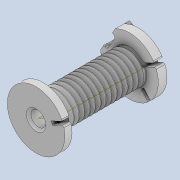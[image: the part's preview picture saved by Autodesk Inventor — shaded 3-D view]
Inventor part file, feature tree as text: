
AUTODESK INVENTOR PART (.ipt)
format: ipt  version: 2020 (Build 240168000, 168)  size: 1,136,128 bytes
history: native  units: mm
features: sketch x14, fillet x13, extrude x12, projected_geometry x12, other x4, thicken_offset x3, chamfer x2, plane x1, sweep x1, reference x1
ambient origin geometry x8: Origin, YZ Plane, XZ Plane, XY Plane, X Axis, Y Axis, Z Axis, Center Point
bodies: Solid1 (feature_tree)
feature tree (63):
  extrude  "Extrusion1"  Depth=12.0mm
  extrude  "Extrusion2"  Depth=3.0mm
  extrude  "Extrusion3"  Depth=18.0mm TaperAngle=0.0deg
  sketch  "3D Sketch1"
  plane  "Work Plane1"
  sweep  "Sweep1"
  extrude  "Extrusion4"  Depth=0.7mm
  extrude  "Extrusion5"  TaperAngle=0.0deg  [1 undecoded]
  fillet  "Fillet1"  Radius=5.0mm
  fillet  "Fillet2"  Radius=0.7mm
  fillet  "Fillet3"  Radius=1.0mm
  fillet  "Fillet4"  Radius=5.0mm
  fillet  "Fillet5"  Radius=0.7mm
  fillet  "Fillet6"  Radius=1.0mm
  extrude  "Extrusion6"  Depth=0.1mm
  thicken_offset  "Thicken1"
  thicken_offset  "Thicken2"
  extrude  "Extrusion7"  Depth=0.1mm
  extrude  "Extrusion8"  Depth=0.1mm
  extrude  "Extrusion9"  Depth=8.0mm
  chamfer  "Chamfer1"  Distance=2.0mm
  fillet  "Fillet7"  Radius=0.8mm
  fillet  "Fillet8"  Radius=0.8mm
  extrude  "Extrusion10"  Depth=0.5mm
  extrude  "Extrusion11"  Depth=0.4mm
  extrude  "Extrusion13"  Depth=0.4mm TaperAngle=0.0deg
  fillet  "Fillet10"  Radius=4.0mm
  fillet  "Fillet11"  Radius=0.8mm
  fillet  "Fillet12"  Radius=0.5mm
  fillet  "Fillet13"  Radius=0.5mm
  fillet  "Fillet14"  Radius=0.5mm
  thicken_offset  "Thicken3"
  chamfer  "Chamfer2"  Distance=3.490659mm
  sketch  "Sketch1"  dims[d0=3.0mm d1=12.0mm]
  reference  "Reference1"
  sketch  "Sketch2"  dims[d2=1.0mm d3=0.0mm d4=3.0mm]
  sketch  "Sketch3"  dims[d5=7.0mm d6=18.0mm d7=0.0mm]
  projected_geometry  "Projected Loop1"
  other  "Helical Curve2"
  sketch  "Sketch4"  dims[d8=1.0mm d9=0.0mm d14=18.0mm d15=160.0mm d16=7.0mm d17=0.0mm]
  projected_geometry  "Projected Loop2"
  projected_geometry  "Projected Loop3"
  sketch  "Sketch5"  dims[d18=0.5mm d19=0.7mm]
  projected_geometry  "Projected Loop4"
  sketch  "Sketch6"  dims[d20=0.5mm d21=0.0mm d22=0.0mm d23=5.0mm d24=0.7mm d25=1.0mm d26=0.0mm d27=5.0mm d28=0.7mm d29=1.0mm d30=0.0mm]
  projected_geometry  "Projected Loop5"
  sketch  "Sketch7"  dims[d31=1.0mm d32=0.1mm]
  projected_geometry  "Projected Loop6"
  sketch  "Sketch8"  dims[d33=0.1mm d34=0.1mm]
  projected_geometry  "Projected Loop7"
  sketch  "Sketch9"  dims[d35=1.0mm d36=0.1mm]
  projected_geometry  "Projected Loop8"
  sketch  "Sketch10"  dims[d37=30.0deg d38=8.0mm]
  projected_geometry  "Projected Loop9"
  sketch  "Sketch11"  dims[d39=6.0mm d40=2.0mm d41=0.0mm d42=0.8mm d43=0.8mm]
  projected_geometry  "Projected Loop10"
  sketch  "Sketch12"  dims[d44=0.5mm d45=0.5mm]
  projected_geometry  "Projected Loop11"
  sketch  "Sketch14"  dims[d46=4.0mm d47=0.0mm d48=1.4mm d49=4.0mm d50=0.0mm d51=4.0mm d52=0.8mm d53=0.0mm d54=0.5mm d55=2.0mm d56=45.0deg d57=0.5mm d58=0.5mm d59=3.490659mm d60=2.2mm d61=0.7mm d62=2.0mm d63=0.0mm d64=5.0mm d65=1.6mm d66=2.0mm d67=0.0mm d72=0.8mm d73=3.0mm d74=5.0mm d75=2.0mm d76=0.0mm d77=1.0mm d78=0.3mm d79=0.1mm d80=0.3mm d81=0.4mm d82=0.05mm d83=0.05mm d84=0.5mm d85=2.0mm d86=45.0deg]
  projected_geometry  "Projected Loop13"
  parser-record x1  (decoder bookkeeping rows leaked as tree rows — omitted from the tree; the rows remain in map.json)
  other  "tip2_ass_t1.iam"
  other  "bearing_3_6_2:1"
note: 1 required parameter value undecoded (feature->parameter linkage not recoverable at this tier; creation-order binding heuristic only, values carry confidence <= 0.55)
note: 1 file-system path scrubbed to <path> (originals preserved in map.json)
